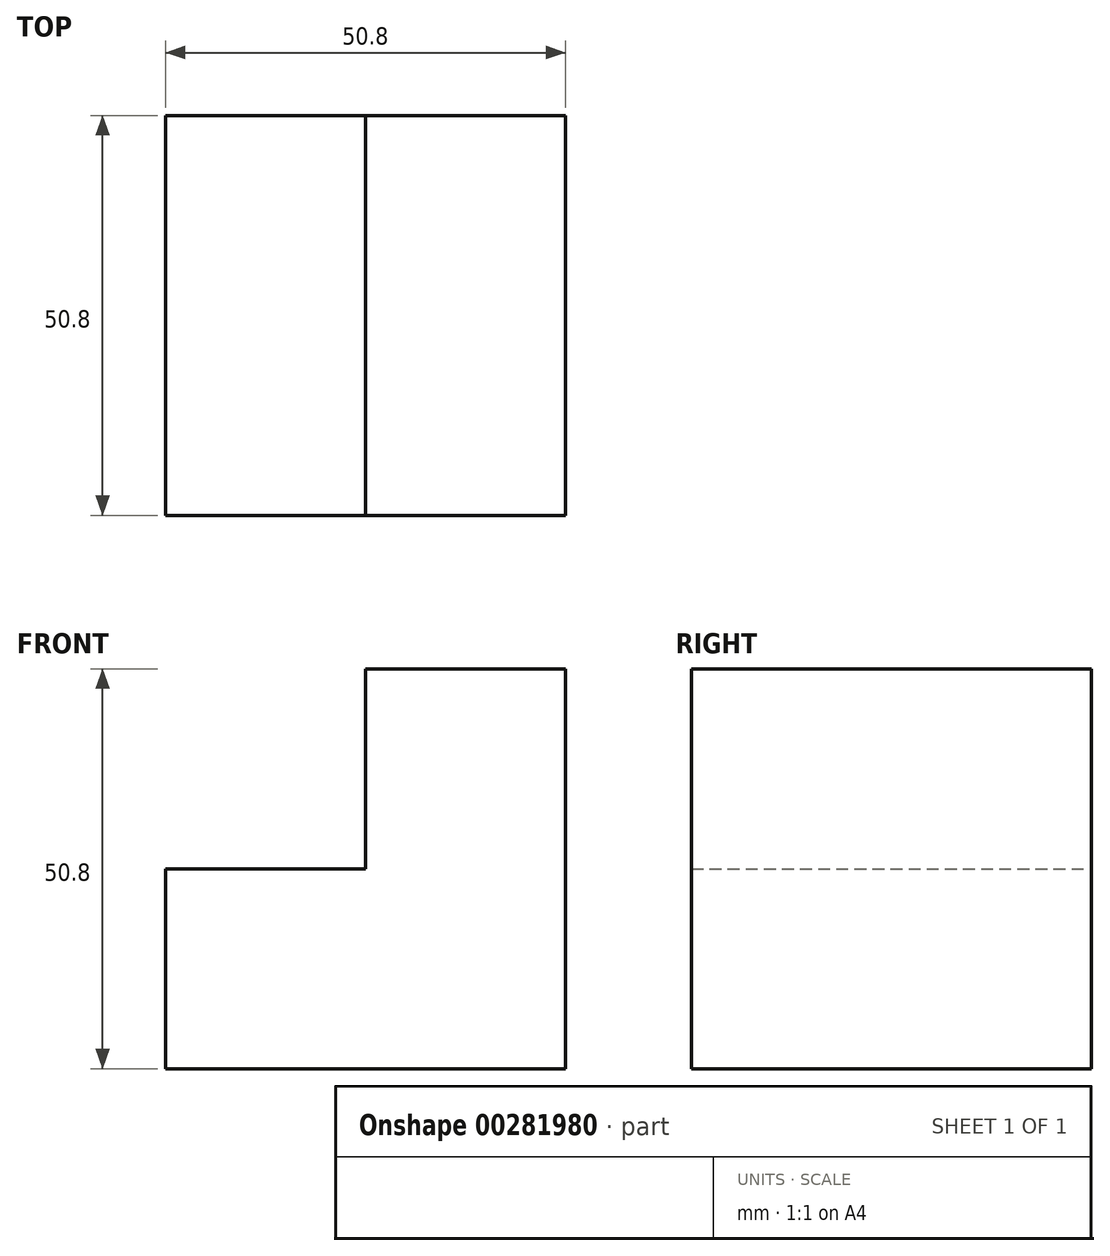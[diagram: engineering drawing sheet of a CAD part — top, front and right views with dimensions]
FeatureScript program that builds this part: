
annotation { "Feature Type Name" : "Feature", "Feature Type Description" : "" }
export const myFeature = defineFeature(function(context is Context, id is Id, definition is map)
    precondition{}
    {
        {
            var Q0;
            Q0=qCreatedBy(makeId("Front.planeOp"),FACE);
            var sketch = newSketch(context, id + "F0", { "sketchPlane" : qUnion([Q0])});
            skLineSegment(sketch, "E0", {"start": v(0, 0) * mm, "end": v(-50.8, 0) * mm});
            skLineSegment(sketch, "E1", {"start": v(-50.8, 0) * mm, "end": v(-50.8, 25.4) * mm});
            skLineSegment(sketch, "E2", {"start": v(-25.4, 25.4) * mm, "end": v(-50.8, 25.4) * mm});
            skLineSegment(sketch, "E3", {"start": v(-25.4, 25.4) * mm, "end": v(-25.4, 50.8) * mm});
            skLineSegment(sketch, "E4", {"start": v(-25.4, 50.8) * mm, "end": v(0, 50.8) * mm});
            skLineSegment(sketch, "E5", {"start": v(0, 50.8) * mm, "end": v(0, 0) * mm});
            skSolve(sketch);
        }
        {
            var Q0;
            Q0 = qSketchRegion(id + "F0", true);
            extrude(context, id + "F1", {"entities" : qUnion([Q0]), "depth" : 50.8 * mm});
        }
    });
